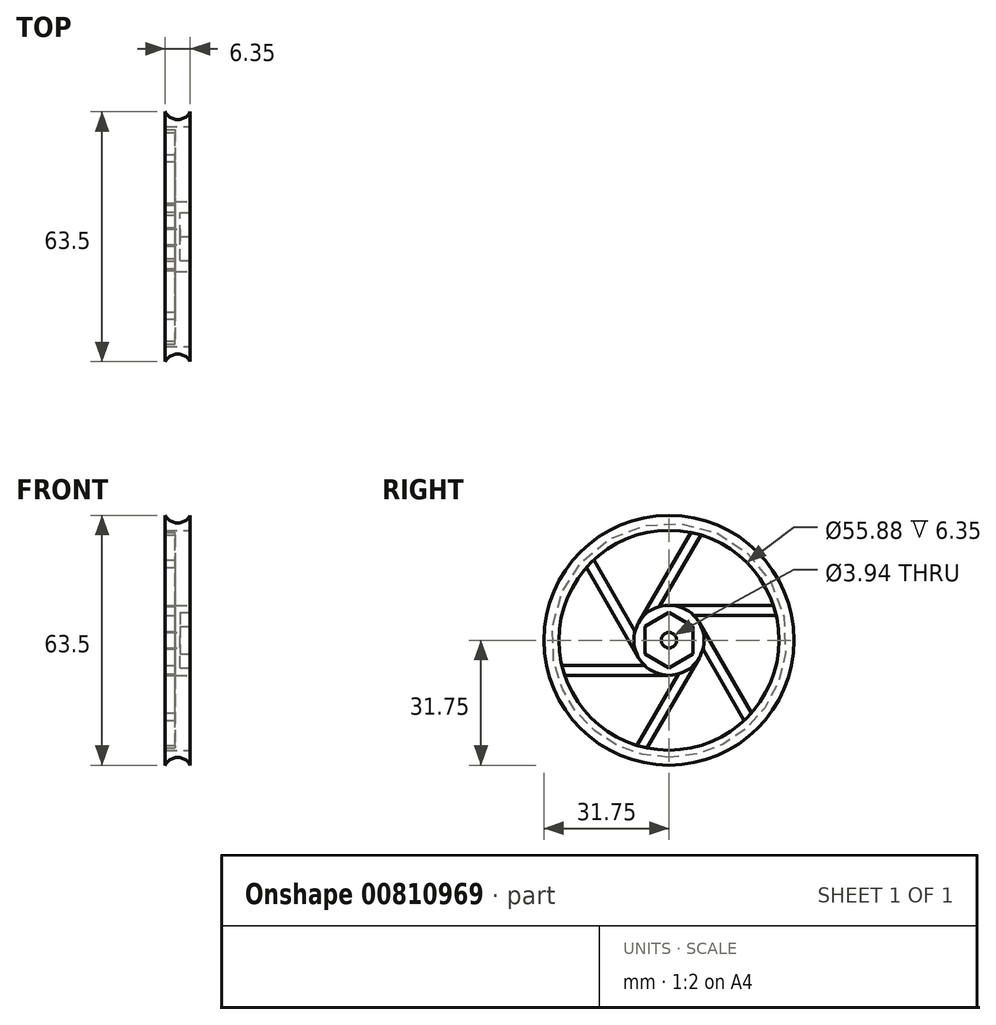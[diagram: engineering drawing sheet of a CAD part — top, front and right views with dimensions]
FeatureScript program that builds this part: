
annotation { "Feature Type Name" : "Feature", "Feature Type Description" : "" }
export const myFeature = defineFeature(function(context is Context, id is Id, definition is map)
    precondition{}
    {
        {
            var Q0;
            Q0=qCreatedBy(makeId("Front.planeOp"),FACE);
            var sketch = newSketch(context, id + "F0", { "sketchPlane" : qUnion([Q0])});
            skLineSegment(sketch, "E0", {"start": v(0, 0) * mm, "end": v(0, 31.75) * mm});
            skArc(sketch, "E1", {"start": v(0, 31.75) * mm, "mid": v(3.17, 29.8) * mm, "end": v(6.35, 31.75) * mm});
            skLineSegment(sketch, "E2", {"start": v(6.35, 31.75) * mm, "end": v(6.35, 27.94) * mm});
            skLineSegment(sketch, "E3", {"start": v(6.35, 27.94) * mm, "end": v(6.35, 0) * mm});
            skLineSegment(sketch, "E4", {"start": v(6.35, 0) * mm, "end": v(0, 0) * mm});
            skLineSegment(sketch, "E5", {"start": v(6.35, 0) * mm, "end": v(6.35, 8.9) * mm});
            skLineSegment(sketch, "E6", {"start": v(6.35, 8.9) * mm, "end": v(2.54, 8.9) * mm});
            skLineSegment(sketch, "E7", {"start": v(2.54, 8.9) * mm, "end": v(2.54, 27.94) * mm});
            skLineSegment(sketch, "E8", {"start": v(2.54, 27.94) * mm, "end": v(6.35, 27.94) * mm});
            skSolve(sketch);
        }
        {
            var Q0;
            Q0=makeQuery(id+"F0.imprint","IMPRINT",FACE,{"disambiguationData":[TD([[makeQuery(id+"F0.imprint","IMPRINT",EDGE,{"derivedFrom":sQuery(id+"F0.wireOp",EDGE,"E0")}),-1.0]])]});
            var Q1;
            Q1=sQuery(id+"F0.wireOp",EDGE,"E4");
            revolve(context, id + "F1", {"surfaceOperationType" : NewSurfaceOperationType.NEW, "entities" : qUnion([Q0]), "axis" : qUnion([Q1]), "revolveType" : RevolveType.FULL});
        }
        {
            var Q0;
            Q0=makeQuery(id+"F1.opRevolve","SWEPT_FACE",FACE,{"disambiguationData":[OSD([sQuery(id+"F0.wireOp",EDGE,"E3")])]});
            var sketch = newSketch(context, id + "F2", { "sketchPlane" : qUnion([Q0])});
            skCircle(sketch, "E9.cCircle", {"center": v(0, 0) * mm, "radius": 6.1 * mm, "construction": true});
            skLineSegment(sketch, "E9.0", {"start": v(6.1, 3.52) * mm, "end": v(6.1, -3.52) * mm});
            skLineSegment(sketch, "E9.1", {"start": v(6.1, -3.52) * mm, "end": v(0, -7.04) * mm});
            skLineSegment(sketch, "E9.2", {"start": v(0, -7.04) * mm, "end": v(-6.1, -3.52) * mm});
            skLineSegment(sketch, "E9.3", {"start": v(-6.1, -3.52) * mm, "end": v(-6.1, 3.52) * mm});
            skLineSegment(sketch, "E9.4", {"start": v(-6.1, 3.52) * mm, "end": v(0, 7.04) * mm});
            skLineSegment(sketch, "E9.5", {"start": v(0, 7.04) * mm, "end": v(6.1, 3.52) * mm});
            skPoint(sketch, "E9.0.midPoint", {"position": v(6.1, 0) * mm});
            skSolve(sketch);
        }
        {
            var Q0;
            Q0=makeQuery(id+"F2.imprint","IMPRINT",FACE,{"disambiguationData":[TD([[makeQuery(id+"F2.imprint","IMPRINT",EDGE,{"derivedFrom":sQuery(id+"F2.wireOp",EDGE,"E9.0")}),-1.0]])]});
            extrude(context, id + "F3", {"entities" : qUnion([Q0]), "operationType" : NewBodyOperationType.REMOVE, "oppositeDirection" : true, "depth" : 2.54 * mm, "offsetDistance" : 25.4 * mm});
        }
        {
            var Q0;
            Q0=makeQuery(id+"F1.opRevolve","SWEPT_FACE",FACE,{"disambiguationData":[OSD([sQuery(id+"F0.wireOp",EDGE,"E7")])]});
            var sketch = newSketch(context, id + "F4", { "sketchPlane" : qUnion([Q0])});
            skLineSegment(sketch, "E10", {"start": v(0, 8.9) * mm, "end": v(26.49, 8.9) * mm});
            skLineSegment(sketch, "E11", {"start": v(26.49, 8.9) * mm, "end": v(27.8, 8.9) * mm});
            skLineSegment(sketch, "E12", {"start": v(27.8, 8.9) * mm, "end": v(27.8, 6.35) * mm});
            skLineSegment(sketch, "E13", {"start": v(27.8, 6.35) * mm, "end": v(6.22, 6.35) * mm});
            skLineSegment(sketch, "E14.1.0", {"start": v(8.4, 27.26) * mm, "end": v(-2.39, 8.56) * mm});
            skLineSegment(sketch, "E14.1.1", {"start": v(-7.7, 4.45) * mm, "end": v(5.55, 27.38) * mm});
            skLineSegment(sketch, "E14.2.0", {"start": v(-19.4, 20.9) * mm, "end": v(-8.61, 2.21) * mm});
            skLineSegment(sketch, "E14.2.1", {"start": v(-7.7, -4.45) * mm, "end": v(-20.94, 18.5) * mm});
            skLineSegment(sketch, "E14.3.0", {"start": v(-27.8, -6.35) * mm, "end": v(-6.22, -6.35) * mm});
            skLineSegment(sketch, "E14.3.1", {"start": v(0, -8.9) * mm, "end": v(-26.49, -8.89) * mm});
            skLineSegment(sketch, "E14.4.0", {"start": v(-8.4, -27.26) * mm, "end": v(2.39, -8.56) * mm});
            skLineSegment(sketch, "E14.4.1", {"start": v(7.7, -4.45) * mm, "end": v(-5.55, -27.38) * mm});
            skLineSegment(sketch, "E14.5.0", {"start": v(19.4, -20.9) * mm, "end": v(8.61, -2.21) * mm});
            skLineSegment(sketch, "E14.5.1", {"start": v(7.7, 4.45) * mm, "end": v(20.94, -18.5) * mm});
            skPoint(sketch, "E14.center", {"position": v(0, 0) * mm});
            skCircle(sketch, "E15", {"center": v(0, 0) * mm, "radius": 1.97 * mm});
            skSolve(sketch);
        }
        {
            var Q0;
            {var subQ0=sQuery(id+"F4.wireOp",EDGE,"E14.1.1");Q0=makeQuery(id+"F4.imprint","IMPRINT",FACE,{"disambiguationData":[TD([[makeQuery(id+"F4.imprint","IMPRINT",EDGE,{"derivedFrom":subQ0}),1.0]])]});}
            var Q1;
            {var subQ0=sQuery(id+"F4.wireOp",EDGE,"E10");Q1=makeQuery(id+"F4.imprint","IMPRINT",FACE,{"disambiguationData":[TD([[makeQuery(id+"F4.imprint","IMPRINT",EDGE,{"derivedFrom":subQ0}),1.0]])]});}
            var Q2;
            {var subQ6=sQuery(id+"F4.wireOp",EDGE,"E14.5.1");Q2=makeQuery(id+"F4.imprint","IMPRINT",FACE,{"disambiguationData":[TD([[makeQuery(id+"F4.imprint","IMPRINT",EDGE,{"derivedFrom":subQ6}),1.0]])]});}
            var Q3;
            {var subQ0=sQuery(id+"F4.wireOp",EDGE,"E14.4.1");Q3=makeQuery(id+"F4.imprint","IMPRINT",FACE,{"disambiguationData":[TD([[makeQuery(id+"F4.imprint","IMPRINT",EDGE,{"derivedFrom":subQ0}),1.0]])]});}
            var Q4;
            {var subQ0=sQuery(id+"F4.wireOp",EDGE,"E14.3.1");Q4=makeQuery(id+"F4.imprint","IMPRINT",FACE,{"disambiguationData":[TD([[makeQuery(id+"F4.imprint","IMPRINT",EDGE,{"derivedFrom":subQ0}),1.0]])]});}
            var Q5;
            {var subQ0=sQuery(id+"F4.wireOp",EDGE,"E14.2.1");Q5=makeQuery(id+"F4.imprint","IMPRINT",FACE,{"disambiguationData":[TD([[makeQuery(id+"F4.imprint","IMPRINT",EDGE,{"derivedFrom":subQ0}),1.0]])]});}
            extrude(context, id + "F5", {"entities" : qUnion([Q0, Q1, Q2, Q3, Q4, Q5]), "operationType" : NewBodyOperationType.REMOVE, "endBound" : BoundingType.THROUGH_ALL, "oppositeDirection" : true, "depth" : 25.4 * mm, "offsetDistance" : 25.4 * mm});
        }
        {
            var Q0;
            Q0=makeQuery(id+"F3.boolean.opBoolean","COPY",FACE,{"derivedFrom":makeQuery(id+"F3.opExtrude","CAP_FACE",FACE,{"disambiguationData":[OSD([sQuery(id+"F2.wireOp",EDGE,"E9.0"),sQuery(id+"F2.wireOp",EDGE,"E9.1"),sQuery(id+"F2.wireOp",EDGE,"E9.2"),sQuery(id+"F2.wireOp",EDGE,"E9.3"),sQuery(id+"F2.wireOp",EDGE,"E9.4"),sQuery(id+"F2.wireOp",EDGE,"E9.5")])],"isStart":false})});
            var sketch = newSketch(context, id + "F6", { "sketchPlane" : qUnion([Q0])});
            skCircle(sketch, "E16", {"center": v(0, 0) * mm, "radius": 1.97 * mm});
            skSolve(sketch);
        }
        {
            var Q0;
            Q0=makeQuery(id+"F6.imprint","IMPRINT",FACE,{"disambiguationData":[TD([[makeQuery(id+"F6.imprint","IMPRINT",EDGE,{"derivedFrom":sQuery(id+"F6.wireOp",EDGE,"E16")}),1.0]])]});
            extrude(context, id + "F7", {"entities" : qUnion([Q0]), "operationType" : NewBodyOperationType.REMOVE, "endBound" : BoundingType.THROUGH_ALL, "oppositeDirection" : true, "depth" : 25.4 * mm, "offsetDistance" : 25.4 * mm});
        }
    });
